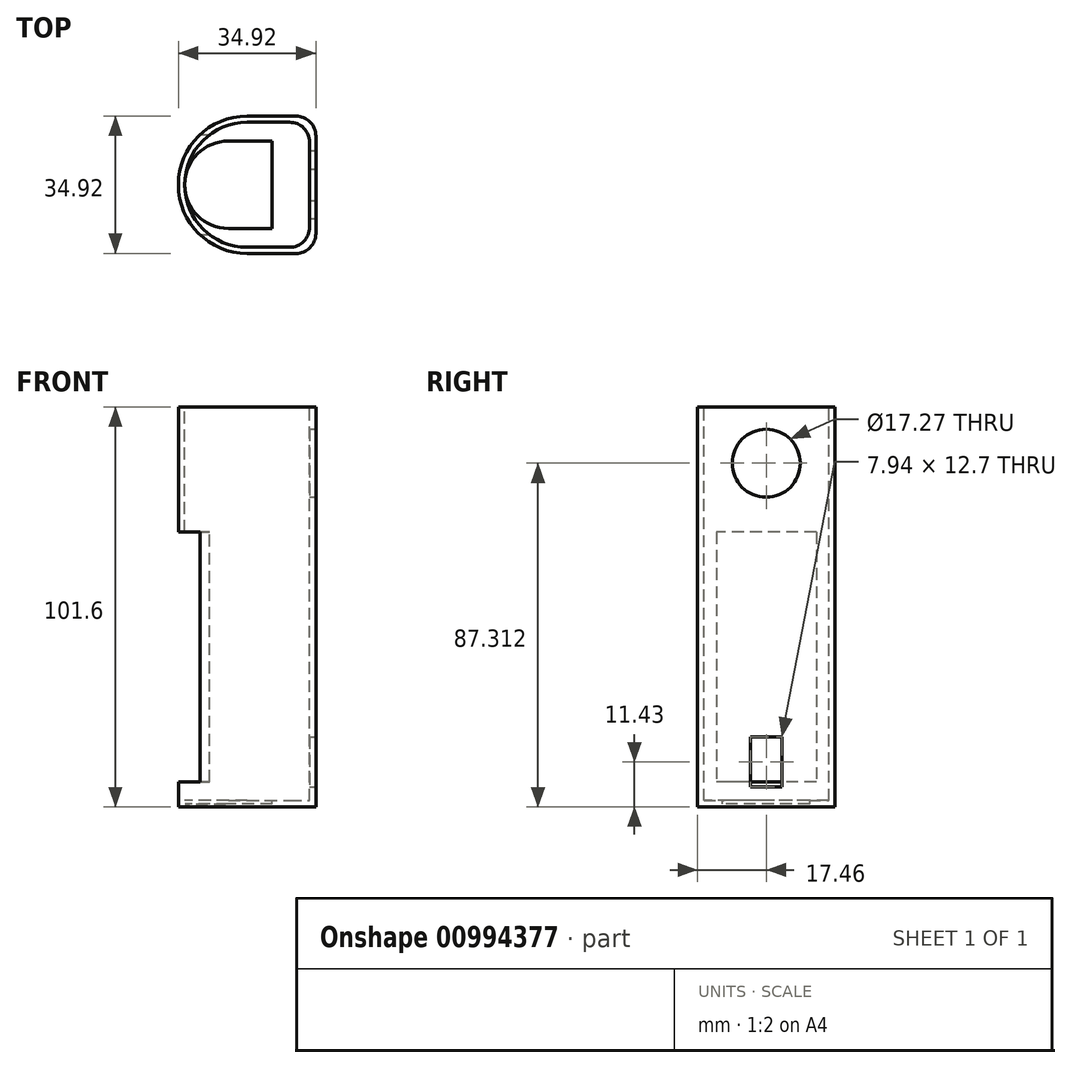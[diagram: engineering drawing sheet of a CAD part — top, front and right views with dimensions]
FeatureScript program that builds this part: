
annotation { "Feature Type Name" : "Feature", "Feature Type Description" : "" }
export const myFeature = defineFeature(function(context is Context, id is Id, definition is map)
    precondition{}
    {
        {
            var Q0;
            Q0=qCreatedBy(makeId("Top.planeOp"),FACE);
            var sketch = newSketch(context, id + "F0", { "sketchPlane" : qUnion([Q0])});
            skCircle(sketch, "E0", {"center": v(0, 0) * mm, "radius": 17.46 * mm});
            skLineSegment(sketch, "E1", {"start": v(0, -17.46) * mm, "end": v(17.46, -17.46) * mm});
            skLineSegment(sketch, "E2", {"start": v(0, 17.46) * mm, "end": v(17.46, 17.46) * mm});
            skPoint(sketch, "E3", {"position": v(17.46, 0) * mm});
            skLineSegment(sketch, "E4", {"start": v(17.46, 17.46) * mm, "end": v(17.46, -17.46) * mm});
            skSolve(sketch);
        }
        {
            var Q0;
            Q0 = qSketchRegion(id + "F0", true);
            extrude(context, id + "F1", {"entities" : qUnion([Q0]), "depth" : 101.6 * mm, "offsetDistance" : 25.4 * mm});
        }
        {
            var Q0;
            Q0=makeQuery(id+"F1.opExtrude","CAP_FACE",FACE,{"disambiguationData":[OSD([sQuery(id+"F0.wireOp",EDGE,"E0"),sQuery(id+"F0.wireOp",EDGE,"E1"),sQuery(id+"F0.wireOp",EDGE,"E2"),sQuery(id+"F0.wireOp",EDGE,"E4")])],"isStart":false});
            var sketch = newSketch(context, id + "F2", { "sketchPlane" : qUnion([Q0])});
            skCircle(sketch, "E5", {"center": v(0, 0) * mm, "radius": 15.88 * mm});
            skLineSegment(sketch, "E6", {"start": v(0, 15.88) * mm, "end": v(15.88, 15.88) * mm});
            skLineSegment(sketch, "E7", {"start": v(15.88, 15.88) * mm, "end": v(15.88, -15.88) * mm});
            skLineSegment(sketch, "E8", {"start": v(15.88, -15.88) * mm, "end": v(0, -15.88) * mm});
            skSolve(sketch);
        }
        {
            var Q0;
            Q0 = qSketchRegion(id + "F2", true);
            extrude(context, id + "F3", {"entities" : qUnion([Q0]), "operationType" : NewBodyOperationType.REMOVE, "oppositeDirection" : true, "depth" : 100.01 * mm, "offsetDistance" : 25.4 * mm});
        }
        {
            var Q0;
            Q0=makeQuery(id+"F1.opExtrude","SWEPT_EDGE",EDGE,{"disambiguationData":[OSD([sQuery(id+"F0.wireOp",EDGE,"E1"),sQuery(id+"F0.wireOp",EDGE,"E4")])]});
            var Q1;
            Q1=makeQuery(id+"F1.opExtrude","SWEPT_EDGE",EDGE,{"disambiguationData":[OSD([sQuery(id+"F0.wireOp",EDGE,"E2"),sQuery(id+"F0.wireOp",EDGE,"E4")])]});
            fillet(context, id + "F4", {"entities" : qUnion([Q0, Q1]), "radius" : 5.08 * mm, "tangentPropagation" : true, "allowEdgeOverflow" : false});
        }
        {
            var Q0;
            Q0=makeQuery(id+"F3.boolean.opBoolean","COPY",EDGE,{"derivedFrom":makeQuery(id+"F3.opExtrude","SWEPT_EDGE",EDGE,{"disambiguationData":[OSD([sQuery(id+"F2.wireOp",EDGE,"E6"),sQuery(id+"F2.wireOp",EDGE,"E7")])]})});
            var Q1;
            Q1=makeQuery(id+"F3.boolean.opBoolean","COPY",EDGE,{"derivedFrom":makeQuery(id+"F3.opExtrude","SWEPT_EDGE",EDGE,{"disambiguationData":[OSD([sQuery(id+"F2.wireOp",EDGE,"E7"),sQuery(id+"F2.wireOp",EDGE,"E8")])]})});
            fillet(context, id + "F5", {"entities" : qUnion([Q0, Q1]), "radius" : 5.08 * mm, "tangentPropagation" : true, "allowEdgeOverflow" : false});
        }
        {
            var Q0;
            Q0=makeQuery(id+"F1.opExtrude","SWEPT_FACE",FACE,{"disambiguationData":[OSD([sQuery(id+"F0.wireOp",EDGE,"E4")])]});
            var sketch = newSketch(context, id + "F6", { "sketchPlane" : qUnion([Q0])});
            skCircle(sketch, "E9", {"center": v(0, 87.31) * mm, "radius": 8.64 * mm});
            skPoint(sketch, "E9.centerSnap0", {"position": v(0, 101.6) * mm});
            skSolve(sketch);
        }
        {
            var Q0;
            Q0 = qSketchRegion(id + "F6", true);
            extrude(context, id + "F7", {"entities" : qUnion([Q0]), "operationType" : NewBodyOperationType.REMOVE, "oppositeDirection" : true, "depth" : 25.4 * mm, "offsetDistance" : 25.4 * mm});
        }
        {
            var Q0;
            Q0=makeQuery(id+"F1.opExtrude","SWEPT_FACE",FACE,{"disambiguationData":[OSD([sQuery(id+"F0.wireOp",EDGE,"E4")])]});
            var sketch = newSketch(context, id + "F8", { "sketchPlane" : qUnion([Q0])});
            skPoint(sketch, "E10", {"position": v(0, 5.08) * mm});
            skLineSegment(sketch, "E11", {"start": v(0, 5.08) * mm, "end": v(-3.97, 5.08) * mm});
            skLineSegment(sketch, "E12", {"start": v(0, 5.08) * mm, "end": v(3.97, 5.08) * mm});
            skLineSegment(sketch, "E13", {"start": v(-3.97, 5.08) * mm, "end": v(-3.97, 17.78) * mm});
            skLineSegment(sketch, "E14", {"start": v(-3.97, 17.78) * mm, "end": v(3.97, 17.78) * mm});
            skLineSegment(sketch, "E15", {"start": v(3.97, 17.78) * mm, "end": v(3.97, 5.08) * mm});
            skSolve(sketch);
        }
        {
            var Q0;
            Q0 = qSketchRegion(id + "F8", true);
            extrude(context, id + "F9", {"entities" : qUnion([Q0]), "operationType" : NewBodyOperationType.REMOVE, "oppositeDirection" : true, "depth" : 25.4 * mm, "offsetDistance" : 25.4 * mm});
        }
        {
            var Q0;
            Q0=qCreatedBy(makeId("Right.planeOp"),FACE);
            var sketch = newSketch(context, id + "F10", { "sketchPlane" : qUnion([Q0])});
            skPoint(sketch, "E16", {"position": v(12.7, 0) * mm});
            skPoint(sketch, "E17", {"position": v(-12.7, 0) * mm});
            skLineSegment(sketch, "E18", {"start": v(12.7, 0) * mm, "end": v(12.7, 69.85) * mm});
            skLineSegment(sketch, "E19", {"start": v(12.7, 69.85) * mm, "end": v(-12.7, 69.85) * mm});
            skLineSegment(sketch, "E20", {"start": v(-12.7, 69.85) * mm, "end": v(-12.7, 0) * mm});
            skLineSegment(sketch, "E21", {"start": v(12.7, 6.35) * mm, "end": v(-12.7, 6.35) * mm});
            skSolve(sketch);
        }
        {
            var Q0;
            Q0 = qSketchRegion(id + "F10", true);
            extrude(context, id + "F11", {"entities" : qUnion([Q0]), "operationType" : NewBodyOperationType.REMOVE, "oppositeDirection" : true, "depth" : 25.4 * mm, "offsetDistance" : 25.4 * mm});
        }
        {
            var Q0;
            Q0=makeQuery(id+"F3.boolean.opBoolean","COPY",FACE,{"derivedFrom":makeQuery(id+"F3.opExtrude","CAP_FACE",FACE,{"disambiguationData":[OSD([sQuery(id+"F2.wireOp",EDGE,"E5"),sQuery(id+"F2.wireOp",EDGE,"E6"),sQuery(id+"F2.wireOp",EDGE,"E7"),sQuery(id+"F2.wireOp",EDGE,"E8")])],"isStart":false})});
            var sketch = newSketch(context, id + "F12", { "sketchPlane" : qUnion([Q0])});
            skArc(sketch, "E22", {"start": v(-4.76, 11.11) * mm, "mid": v(-15.88, 0) * mm, "end": v(-4.76, -11.11) * mm});
            skLineSegment(sketch, "E23", {"start": v(-4.76, 11.11) * mm, "end": v(6.35, 11.11) * mm});
            skLineSegment(sketch, "E24", {"start": v(6.35, 11.11) * mm, "end": v(6.35, -11.11) * mm});
            skLineSegment(sketch, "E25", {"start": v(6.35, -11.11) * mm, "end": v(-4.76, -11.11) * mm});
            skSolve(sketch);
        }
        {
            var Q0;
            Q0 = qSketchRegion(id + "F12", true);
            extrude(context, id + "F13", {"entities" : qUnion([Q0]), "operationType" : NewBodyOperationType.REMOVE, "oppositeDirection" : true, "depth" : 0.8 * mm, "offsetDistance" : 25.4 * mm});
        }
    });
